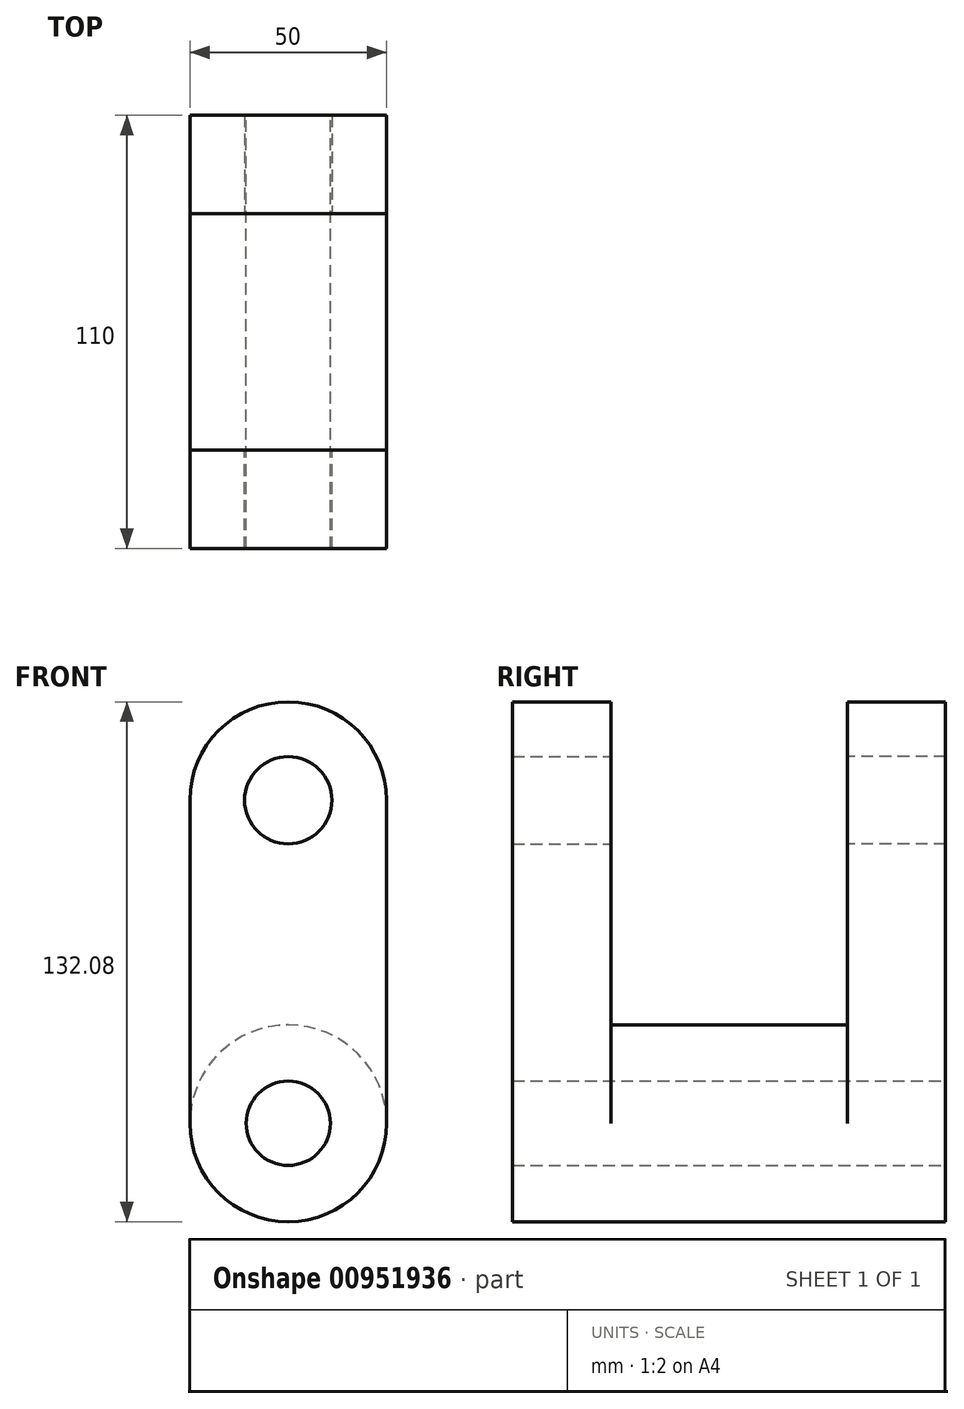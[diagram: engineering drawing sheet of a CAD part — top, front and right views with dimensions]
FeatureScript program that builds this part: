
annotation { "Feature Type Name" : "Feature", "Feature Type Description" : "" }
export const myFeature = defineFeature(function(context is Context, id is Id, definition is map)
    precondition{}
    {
        {
            var Q0;
            Q0=qCreatedBy(makeId("Front.planeOp"),FACE);
            var sketch = newSketch(context, id + "F0", { "sketchPlane" : qUnion([Q0])});
            skArc(sketch, "E0", {"start": v(-25, -24.92) * mm, "mid": v(-0.04, -50) * mm, "end": v(25, -25) * mm});
            skArc(sketch, "E1", {"start": v(25, 57.08) * mm, "mid": v(0, 82.08) * mm, "end": v(-25, 57.08) * mm});
            skLineSegment(sketch, "E2", {"start": v(-25, -24.92) * mm, "end": v(-25, -25) * mm});
            skLineSegment(sketch, "E3", {"start": v(25, -25) * mm, "end": v(25, 57.08) * mm});
            skLineSegment(sketch, "E4", {"start": v(-25, -24.92) * mm, "end": v(-25, 57.08) * mm});
            skCircle(sketch, "E5", {"center": v(0, 57.08) * mm, "radius": 11.1 * mm});
            skCircle(sketch, "E6", {"center": v(0, -25) * mm, "radius": 25 * mm});
            skCircle(sketch, "E7", {"center": v(0, -25) * mm, "radius": 10.7 * mm});
            skSolve(sketch);
        }
        {
            var Q0;
            Q0=makeQuery(id+"F0.imprint","IMPRINT",FACE,{"disambiguationData":[TD([[makeQuery(id+"F0.imprint","IMPRINT",EDGE,{"derivedFrom":sQuery(id+"F0.wireOp",EDGE,"E1")}),1.0]])]});
            var Q1;
            {var subQ0=sQuery(id+"F0.wireOp",EDGE,"E6");var subQ1=makeQuery(id+"F0.imprint","INTERSECT",VERTEX,{"derivedFrom":[sQuery(id+"F0.wireOp",EDGE,"E3"),subQ0]});Q1=makeQuery(id+"F0.imprint","IMPRINT",FACE,{"disambiguationData":[TD([[makeQuery(id+"F0.imprint","IMPRINT",EDGE,{"disambiguationData":[TD([[subQ1,-1.0]])],"derivedFrom":subQ0}),1.0]])]});}
            extrude(context, id + "F1", {"entities" : qUnion([Q0, Q1]), "depth" : 25 * mm, "offsetDistance" : 25 * mm});
        }
        {
            var Q0;
            {var subQ0=sQuery(id+"F0.wireOp",EDGE,"E6");var subQ1=makeQuery(id+"F0.imprint","INTERSECT",VERTEX,{"derivedFrom":[sQuery(id+"F0.wireOp",EDGE,"E3"),subQ0]});Q0=makeQuery(id+"F0.imprint","IMPRINT",FACE,{"disambiguationData":[TD([[makeQuery(id+"F0.imprint","IMPRINT",EDGE,{"disambiguationData":[TD([[subQ1,-1.0]])],"derivedFrom":subQ0}),1.0]])]});}
            extrude(context, id + "F2", {"entities" : qUnion([Q0]), "operationType" : NewBodyOperationType.ADD, "oppositeDirection" : true, "depth" : 30 * mm, "offsetDistance" : 25 * mm});
        }
        {
            var Q0;
            Q0=makeQuery(id+"F1.opExtrude","SWEPT_BODY",BODY,{"disambiguationData":[OSD([sQuery(id+"F0.wireOp",EDGE,"E1"),sQuery(id+"F0.wireOp",EDGE,"E3"),sQuery(id+"F0.wireOp",EDGE,"E4"),sQuery(id+"F0.wireOp",EDGE,"E5"),sQuery(id+"F0.wireOp",EDGE,"E6"),sQuery(id+"F0.wireOp",EDGE,"E7")])]});
            var Q1;
            Q1=makeQuery(id+"F2.opExtrude","CAP_FACE",FACE,{"disambiguationData":[OSD([sQuery(id+"F0.wireOp",EDGE,"E6"),sQuery(id+"F0.wireOp",EDGE,"E7")])],"isStart":false});
            mirror(context, id + "F3", {"operationType" : NewBodyOperationType.ADD, "entities" : qUnion([Q0]), "mirrorPlane" : qUnion([Q1])});
        }
    });
